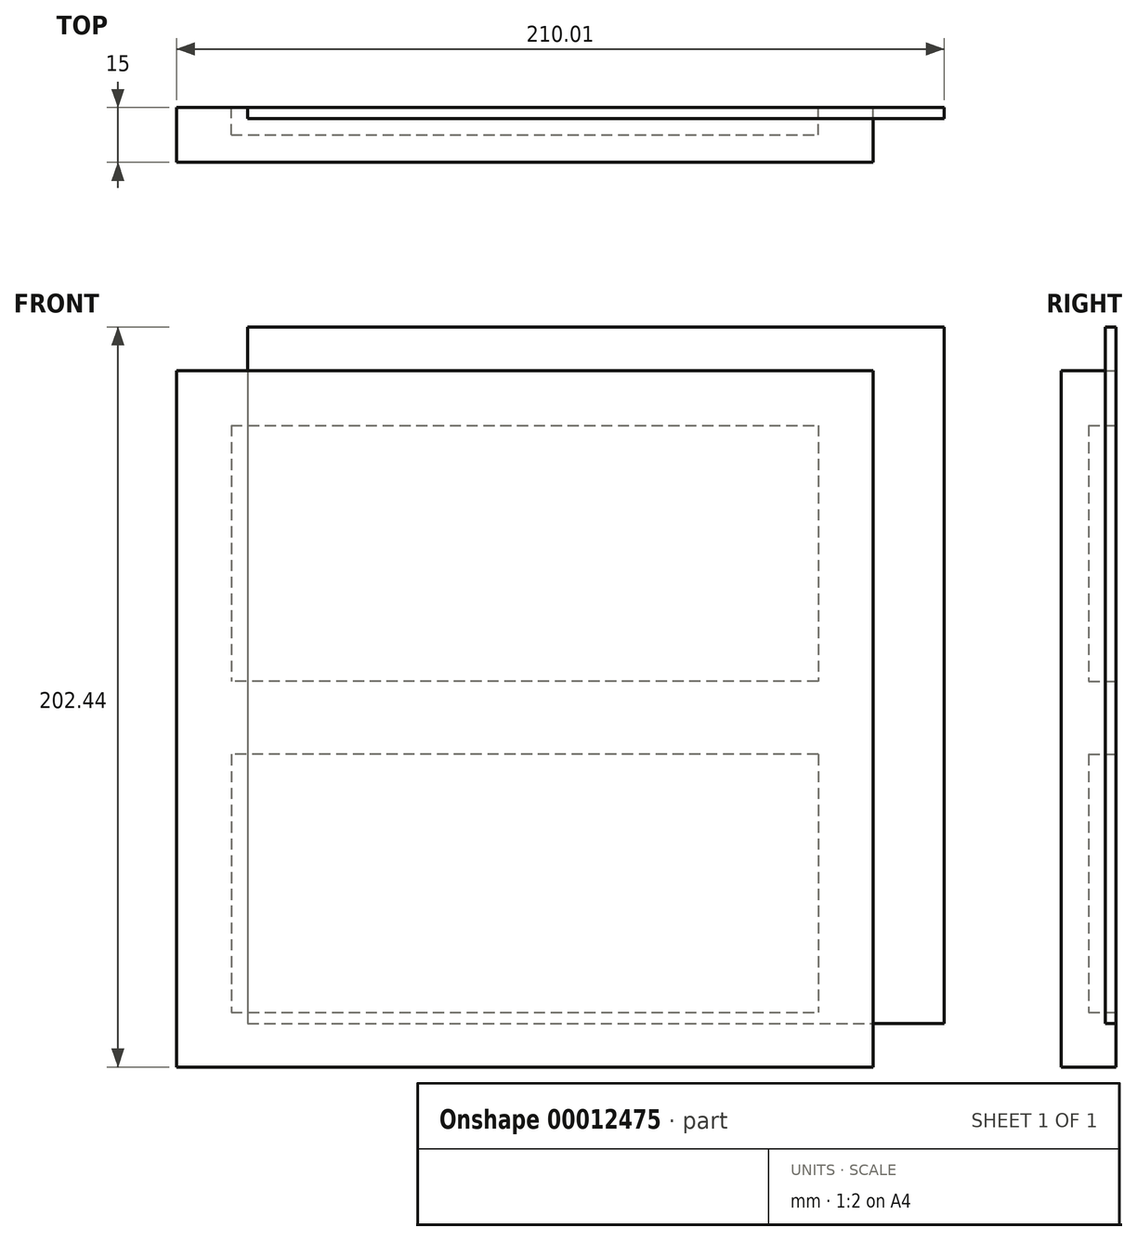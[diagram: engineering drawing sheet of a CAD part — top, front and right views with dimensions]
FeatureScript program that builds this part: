
annotation { "Feature Type Name" : "Feature", "Feature Type Description" : "" }
export const myFeature = defineFeature(function(context is Context, id is Id, definition is map)
    precondition{}
    {
        {
            var Q0;
            Q0=qCreatedBy(makeId("Front.planeOp"),FACE);
            var sketch = newSketch(context, id + "F0", { "sketchPlane" : qUnion([Q0])});
            skLineSegment(sketch, "E0.bottom", {"start": v(-135.29, 77.33) * mm, "end": v(55.21, 77.33) * mm});
            skLineSegment(sketch, "E0.top", {"start": v(-135.29, -113.17) * mm, "end": v(55.21, -113.17) * mm});
            skLineSegment(sketch, "E0.left", {"start": v(-135.29, 77.33) * mm, "end": v(-135.29, -113.17) * mm});
            skLineSegment(sketch, "E0.right", {"start": v(55.21, 77.33) * mm, "end": v(55.21, -113.17) * mm});
            skLineSegment(sketch, "E1.0", {"start": v(-120.29, 62.33) * mm, "end": v(40.21, 62.33) * mm});
            skLineSegment(sketch, "E1.1", {"start": v(-120.29, 62.33) * mm, "end": v(-120.29, -98.17) * mm});
            skLineSegment(sketch, "E1.2", {"start": v(-120.29, -98.17) * mm, "end": v(40.21, -98.17) * mm});
            skLineSegment(sketch, "E1.3", {"start": v(40.21, 62.33) * mm, "end": v(40.21, -98.17) * mm});
            skLineSegment(sketch, "E2.right", {"start": v(40.21, -17.92) * mm, "end": v(40.21, -17.92) * mm});
            skLineSegment(sketch, "E3.0", {"start": v(44.71, -7.67) * mm, "end": v(-120.29, -7.67) * mm});
            skLineSegment(sketch, "E4.0", {"start": v(44.71, -27.67) * mm, "end": v(-120.29, -27.67) * mm});
            skSolve(sketch);
        }
        {
            var Q0;
            {var subQ0=sQuery(id+"F0.wireOp",EDGE,"82b1a075-c616-4b02-a83e-0bbecf219f74.0");var subQ3=sQuery(id+"F0.wireOp",EDGE,"E3.0");var subQ4=makeQuery(id+"F0.imprint","INTERSECT",VERTEX,{"derivedFrom":[subQ3,subQ0]});Q0=makeQuery(id+"F0.imprint","IMPRINT",FACE,{"disambiguationData":[TD([[makeQuery(id+"F0.imprint","IMPRINT",EDGE,{"disambiguationData":[TD([[subQ4,-1.0]])],"derivedFrom":subQ3}),1.0]])]});}
            var Q1;
            {var subQ3=sQuery(id+"F0.wireOp",EDGE,"E1.2");var subQ5=sQuery(id+"F0.wireOp",EDGE,"E1.3");var subQ7=makeQuery(id+"F0.imprint","INTERSECT",VERTEX,{"derivedFrom":[subQ3,subQ5]});Q1=makeQuery(id+"F0.imprint","IMPRINT",FACE,{"disambiguationData":[TD([[makeQuery(id+"F0.imprint","IMPRINT",EDGE,{"disambiguationData":[TD([[subQ7,1.0]])],"derivedFrom":subQ3}),1.0]])]});}
            var Q2;
            {var subQ0=sQuery(id+"F0.wireOp",EDGE,"7a8a59b5-d194-4f77-ada4-d8c736da3c13.0");var subQ3=sQuery(id+"F0.wireOp",EDGE,"E1.2");var subQ4=makeQuery(id+"F0.imprint","INTERSECT",VERTEX,{"derivedFrom":[subQ3,subQ0]});Q2=makeQuery(id+"F0.imprint","IMPRINT",FACE,{"disambiguationData":[TD([[makeQuery(id+"F0.imprint","IMPRINT",EDGE,{"disambiguationData":[TD([[subQ4,-1.0]])],"derivedFrom":subQ3}),1.0]])]});}
            var Q3;
            {var subQ3=sQuery(id+"F0.wireOp",EDGE,"E1.0");var subQ5=sQuery(id+"F0.wireOp",EDGE,"7a8a59b5-d194-4f77-ada4-d8c736da3c13.0");var subQ7=makeQuery(id+"F0.imprint","INTERSECT",VERTEX,{"derivedFrom":[subQ3,subQ5]});Q3=makeQuery(id+"F0.imprint","IMPRINT",FACE,{"disambiguationData":[TD([[makeQuery(id+"F0.imprint","IMPRINT",EDGE,{"disambiguationData":[TD([[subQ7,-1.0]])],"derivedFrom":subQ3}),-1.0]])]});}
            var Q4;
            {var subQ3=sQuery(id+"F0.wireOp",EDGE,"E1.0");var subQ5=sQuery(id+"F0.wireOp",EDGE,"E1.3");var subQ7=makeQuery(id+"F0.imprint","INTERSECT",VERTEX,{"derivedFrom":[subQ3,subQ5]});Q4=makeQuery(id+"F0.imprint","IMPRINT",FACE,{"disambiguationData":[TD([[makeQuery(id+"F0.imprint","IMPRINT",EDGE,{"disambiguationData":[TD([[subQ7,1.0]])],"derivedFrom":subQ3}),-1.0]])]});}
            var Q5;
            {var subQ3=sQuery(id+"F0.wireOp",EDGE,"E1.2");var subQ5=sQuery(id+"F0.wireOp",EDGE,"E1.1");var subQ7=makeQuery(id+"F0.imprint","INTERSECT",VERTEX,{"derivedFrom":[subQ5,subQ3]});Q5=makeQuery(id+"F0.imprint","IMPRINT",FACE,{"disambiguationData":[TD([[makeQuery(id+"F0.imprint","IMPRINT",EDGE,{"disambiguationData":[TD([[subQ7,1.0]])],"derivedFrom":subQ5}),1.0]])]});}
            var Q6;
            {var subQ3=sQuery(id+"F0.wireOp",EDGE,"E3.0");var subQ5=sQuery(id+"F0.wireOp",EDGE,"E1.1");var subQ7=makeQuery(id+"F0.imprint","INTERSECT",VERTEX,{"derivedFrom":[subQ5,subQ3]});Q6=makeQuery(id+"F0.imprint","IMPRINT",FACE,{"disambiguationData":[TD([[makeQuery(id+"F0.imprint","IMPRINT",EDGE,{"disambiguationData":[TD([[subQ7,-1.0]])],"derivedFrom":subQ5}),1.0]])]});}
            var Q7;
            {var subQ3=sQuery(id+"F0.wireOp",EDGE,"E3.0");var subQ5=sQuery(id+"F0.wireOp",EDGE,"E1.3");var subQ7=makeQuery(id+"F0.imprint","INTERSECT",VERTEX,{"derivedFrom":[subQ5,subQ3]});Q7=makeQuery(id+"F0.imprint","IMPRINT",FACE,{"disambiguationData":[TD([[makeQuery(id+"F0.imprint","IMPRINT",EDGE,{"disambiguationData":[TD([[subQ7,-1.0]])],"derivedFrom":subQ5}),-1.0]])]});}
            var Q8;
            {var subQ3=sQuery(id+"F0.wireOp",EDGE,"E1.0");var subQ5=sQuery(id+"F0.wireOp",EDGE,"E1.1");var subQ7=makeQuery(id+"F0.imprint","INTERSECT",VERTEX,{"derivedFrom":[subQ3,subQ5]});Q8=makeQuery(id+"F0.imprint","IMPRINT",FACE,{"disambiguationData":[TD([[makeQuery(id+"F0.imprint","IMPRINT",EDGE,{"disambiguationData":[TD([[subQ7,-1.0]])],"derivedFrom":subQ3}),-1.0]])]});}
            var Q9;
            Q9=makeQuery(id+"F0.imprint","IMPRINT",FACE,{"disambiguationData":[TD([[makeQuery(id+"F0.imprint","IMPRINT",EDGE,{"derivedFrom":sQuery(id+"F0.wireOp",EDGE,"E0.bottom")}),-1.0]])]});
            extrude(context, id + "F1", {"entities" : qUnion([Q0, Q1, Q2, Q3, Q4, Q5, Q6, Q7, Q8, Q9]), "depth" : 15 * mm});
        }
        {
            var Q0;
            {var subQ3=sQuery(id+"F0.wireOp",EDGE,"E1.2");var subQ5=sQuery(id+"F0.wireOp",EDGE,"E1.3");var subQ7=makeQuery(id+"F0.imprint","INTERSECT",VERTEX,{"derivedFrom":[subQ3,subQ5]});Q0=makeQuery(id+"F0.imprint","IMPRINT",FACE,{"disambiguationData":[TD([[makeQuery(id+"F0.imprint","IMPRINT",EDGE,{"disambiguationData":[TD([[subQ7,1.0]])],"derivedFrom":subQ3}),1.0]])]});}
            var Q1;
            {var subQ3=sQuery(id+"F0.wireOp",EDGE,"E1.0");var subQ5=sQuery(id+"F0.wireOp",EDGE,"E1.3");var subQ7=makeQuery(id+"F0.imprint","INTERSECT",VERTEX,{"derivedFrom":[subQ3,subQ5]});Q1=makeQuery(id+"F0.imprint","IMPRINT",FACE,{"disambiguationData":[TD([[makeQuery(id+"F0.imprint","IMPRINT",EDGE,{"disambiguationData":[TD([[subQ7,1.0]])],"derivedFrom":subQ3}),-1.0]])]});}
            var Q2;
            {var subQ3=sQuery(id+"F0.wireOp",EDGE,"E1.0");var subQ5=sQuery(id+"F0.wireOp",EDGE,"E1.1");var subQ7=makeQuery(id+"F0.imprint","INTERSECT",VERTEX,{"derivedFrom":[subQ3,subQ5]});Q2=makeQuery(id+"F0.imprint","IMPRINT",FACE,{"disambiguationData":[TD([[makeQuery(id+"F0.imprint","IMPRINT",EDGE,{"disambiguationData":[TD([[subQ7,-1.0]])],"derivedFrom":subQ3}),-1.0]])]});}
            var Q3;
            {var subQ3=sQuery(id+"F0.wireOp",EDGE,"E1.2");var subQ5=sQuery(id+"F0.wireOp",EDGE,"E1.1");var subQ7=makeQuery(id+"F0.imprint","INTERSECT",VERTEX,{"derivedFrom":[subQ5,subQ3]});Q3=makeQuery(id+"F0.imprint","IMPRINT",FACE,{"disambiguationData":[TD([[makeQuery(id+"F0.imprint","IMPRINT",EDGE,{"disambiguationData":[TD([[subQ7,1.0]])],"derivedFrom":subQ5}),1.0]])]});}
            extrude(context, id + "F2", {"entities" : qUnion([Q0, Q1, Q2, Q3]), "operationType" : NewBodyOperationType.REMOVE, "depth" : 7.5 * mm});
        }
        {
            var Q0;
            Q0=qCreatedBy(makeId("Front.planeOp"),FACE);
            var sketch = newSketch(context, id + "F3", { "sketchPlane" : qUnion([Q0])});
            skLineSegment(sketch, "E5.bottom", {"start": v(-115.78, 89.27) * mm, "end": v(74.72, 89.27) * mm});
            skLineSegment(sketch, "E5.top", {"start": v(-115.78, -101.23) * mm, "end": v(74.72, -101.23) * mm});
            skLineSegment(sketch, "E5.left", {"start": v(-115.78, 89.27) * mm, "end": v(-115.78, -101.23) * mm});
            skLineSegment(sketch, "E5.right", {"start": v(74.72, 89.27) * mm, "end": v(74.72, -101.23) * mm});
            skSolve(sketch);
        }
        {
            var Q0;
            Q0 = qSketchRegion(id + "F3", true);
            extrude(context, id + "F4", {"entities" : qUnion([Q0]), "depth" : 3 * mm});
        }
    });
